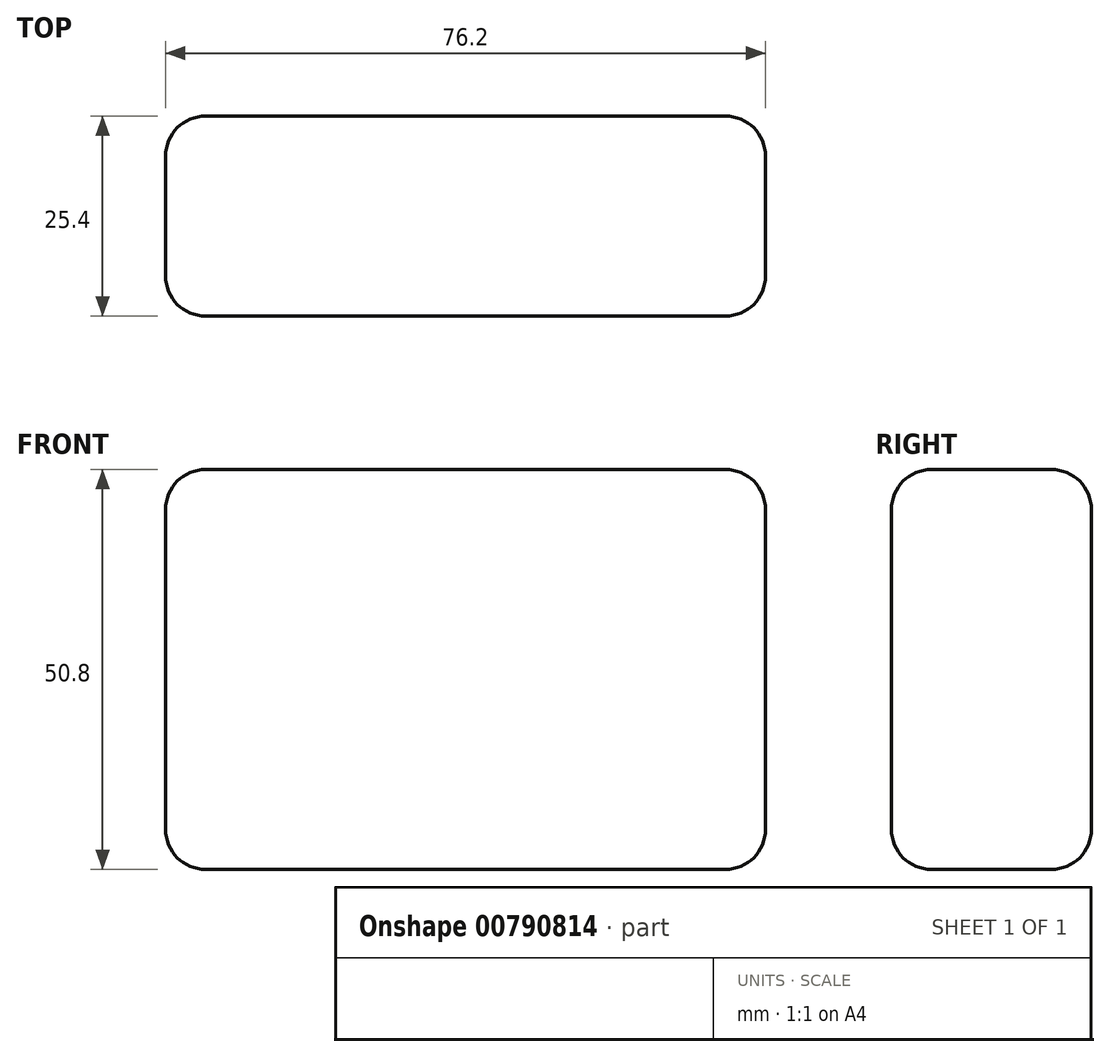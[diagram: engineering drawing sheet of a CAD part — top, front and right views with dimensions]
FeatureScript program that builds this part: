
annotation { "Feature Type Name" : "Feature", "Feature Type Description" : "" }
export const myFeature = defineFeature(function(context is Context, id is Id, definition is map)
    precondition{}
    {
        {
            var Q0;
            Q0=qCreatedBy(makeId("Front.planeOp"),FACE);
            var sketch = newSketch(context, id + "F0", { "sketchPlane" : qUnion([Q0])});
            skLineSegment(sketch, "E0.bottom", {"start": v(38.1, 0) * mm, "end": v(-38.1, 0) * mm});
            skLineSegment(sketch, "E0.top", {"start": v(38.1, 50.8) * mm, "end": v(-38.1, 50.8) * mm});
            skLineSegment(sketch, "E0.left", {"start": v(38.1, 0) * mm, "end": v(38.1, 50.8) * mm});
            skLineSegment(sketch, "E0.right", {"start": v(-38.1, 0) * mm, "end": v(-38.1, 50.8) * mm});
            skLineSegment(sketch, "E1", {"start": v(0, 50.8) * mm, "end": v(0, 0) * mm, "construction": true});
            skSolve(sketch);
        }
        {
            var Q0;
            Q0=makeQuery(id+"F0.imprint","IMPRINT",FACE,{"disambiguationData":[TD([[makeQuery(id+"F0.imprint","IMPRINT",EDGE,{"derivedFrom":sQuery(id+"F0.wireOp",EDGE,"E0.bottom")}),-1.0]])]});
            extrude(context, id + "F1", {"entities" : qUnion([Q0]), "depth" : 25.4 * mm, "offsetDistance" : 25.4 * mm});
        }
        {
            var Q0;
            Q0=makeQuery(id+"F1.opExtrude","SWEPT_FACE",FACE,{"disambiguationData":[OSD([sQuery(id+"F0.wireOp",EDGE,"E0.top")])]});
            var Q1;
            Q1=makeQuery(id+"F1.opExtrude","CAP_FACE",FACE,{"disambiguationData":[OSD([sQuery(id+"F0.wireOp",EDGE,"E0.bottom"),sQuery(id+"F0.wireOp",EDGE,"E0.top"),sQuery(id+"F0.wireOp",EDGE,"E0.left"),sQuery(id+"F0.wireOp",EDGE,"E0.right")])],"isStart":false});
            var Q2;
            Q2=makeQuery(id+"F1.opExtrude","SWEPT_FACE",FACE,{"disambiguationData":[OSD([sQuery(id+"F0.wireOp",EDGE,"E0.left")])]});
            var Q3;
            Q3=makeQuery(id+"F1.opExtrude","CAP_FACE",FACE,{"disambiguationData":[OSD([sQuery(id+"F0.wireOp",EDGE,"E0.bottom"),sQuery(id+"F0.wireOp",EDGE,"E0.top"),sQuery(id+"F0.wireOp",EDGE,"E0.left"),sQuery(id+"F0.wireOp",EDGE,"E0.right")])],"isStart":true});
            var Q4;
            Q4=makeQuery(id+"F1.opExtrude","SWEPT_FACE",FACE,{"disambiguationData":[OSD([sQuery(id+"F0.wireOp",EDGE,"E0.bottom")])]});
            var Q5;
            Q5=makeQuery(id+"F1.opExtrude","SWEPT_FACE",FACE,{"disambiguationData":[OSD([sQuery(id+"F0.wireOp",EDGE,"E0.right")])]});
            fillet(context, id + "F2", {"entities" : qUnion([Q0, Q1, Q2, Q3, Q4, Q5]), "radius" : 5.08 * mm, "tangentPropagation" : true, "allowEdgeOverflow" : false});
        }
    });
